# Revit family: FU_Chair_Sandler_Inga 1-2
name_source: partatom
category: Furniture
units: mm (PartAtom-declared; Revit-internal decimal feet)

## family parameters
Always vertical = Yes
Cut with Voids When Loaded = No
OmniClass Number = 23.40.20.00
OmniClass Title = General Furniture and Specialties
Room Calculation Point = No
Shared = No
Work Plane-Based = No

## types (1)
- Inga 1.2
    Default Elevation = 0 mm  [stored 0 ft]
    Depth = 505 mm  [stored 1.65682 ft]
    Description = Stackable side chair with wooden seat and back on a solid beech frame.
    Frame = Wood -  Aniline - White
    Height = 850 mm  [stored 2.78871 ft]
    Manufacturer = Sandler
    Model = Inga 1.2
    Seat = Wood -  Aniline - White
    URL = https://www.sandlerseating.com
    Width = 465 mm  [stored 1.52559 ft]

note: [stored X ft] marks values corroborated as IEEE doubles in the binary element streams (Revit-internal decimal feet)

## geometry (parser evidence)
native form markers: Sweep x6
no freeform markers — native parametric forms only
